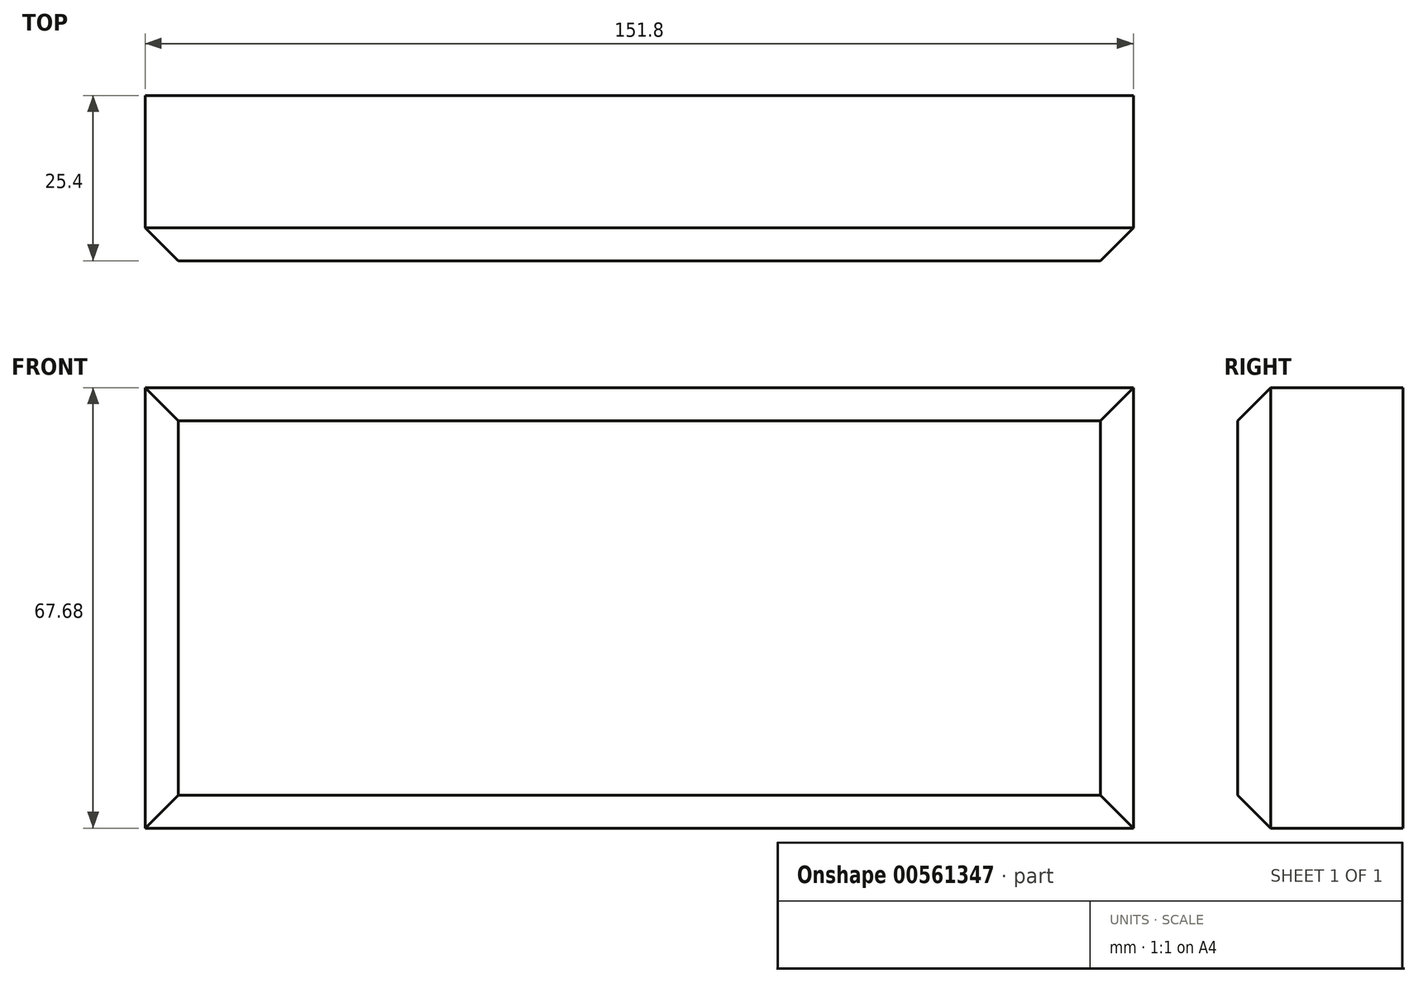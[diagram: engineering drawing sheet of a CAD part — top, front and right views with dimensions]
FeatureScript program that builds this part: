
annotation { "Feature Type Name" : "Feature", "Feature Type Description" : "" }
export const myFeature = defineFeature(function(context is Context, id is Id, definition is map)
    precondition{}
    {
        {
            var Q0;
            Q0=qCreatedBy(makeId("Front.planeOp"),FACE);
            var sketch = newSketch(context, id + "F0", { "sketchPlane" : qUnion([Q0])});
            skLineSegment(sketch, "E0", {"start": v(-76.06, 0) * mm, "end": v(-76.06, 50.76) * mm});
            skLineSegment(sketch, "E1", {"start": v(-76.06, 50.76) * mm, "end": v(75.74, 50.76) * mm});
            skLineSegment(sketch, "E2", {"start": v(75.74, 50.76) * mm, "end": v(75.74, 0) * mm});
            skLineSegment(sketch, "E3", {"start": v(75.74, 0) * mm, "end": v(75.74, -16.92) * mm});
            skLineSegment(sketch, "E4", {"start": v(75.74, -16.92) * mm, "end": v(-76.06, -16.92) * mm});
            skLineSegment(sketch, "E5", {"start": v(-76.06, -16.92) * mm, "end": v(-76.06, 0) * mm});
            skSolve(sketch);
        }
        {
            var Q0;
            Q0=makeQuery(id+"F0.imprint","IMPRINT",FACE,{"disambiguationData":[TD([[makeQuery(id+"F0.imprint","IMPRINT",EDGE,{"derivedFrom":sQuery(id+"F0.wireOp",EDGE,"E0")}),-1.0]])]});
            extrude(context, id + "F1", {"entities" : qUnion([Q0]), "depth" : 25.4 * mm, "offsetDistance" : 25.4 * mm});
        }
        {
            var Q0;
            Q0=makeQuery(id+"F1.opExtrude","CAP_FACE",FACE,{"disambiguationData":[OSD([sQuery(id+"F0.wireOp",EDGE,"E0"),sQuery(id+"F0.wireOp",EDGE,"E1"),sQuery(id+"F0.wireOp",EDGE,"E2"),sQuery(id+"F0.wireOp",EDGE,"E3"),sQuery(id+"F0.wireOp",EDGE,"E4"),sQuery(id+"F0.wireOp",EDGE,"E5")])],"isStart":false});
            chamfer(context, id + "F2", {"entities" : qUnion([Q0]), "width" : 5.08 * mm, "tangentPropagation" : true});
        }
    });
